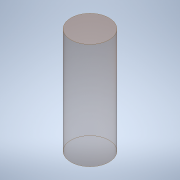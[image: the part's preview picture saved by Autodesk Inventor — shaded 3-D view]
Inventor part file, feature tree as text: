
AUTODESK INVENTOR PART (.ipt)
format: ipt  version: 2020.2 (Build 242310000, 310)  size: 92,160 bytes
history: native  units: mm
features: other x1, extrude x1, sketch x1
ambient origin geometry x8: Origin, YZ Plane, XZ Plane, XY Plane, X Axis, Y Axis, Z Axis, Center Point
bodies: Body1 (feature_tree)
feature tree (3):
  other  "ソリッド1"
  extrude  "押し出し1"  Depth=18.0mm
  sketch  "スケッチ1"
